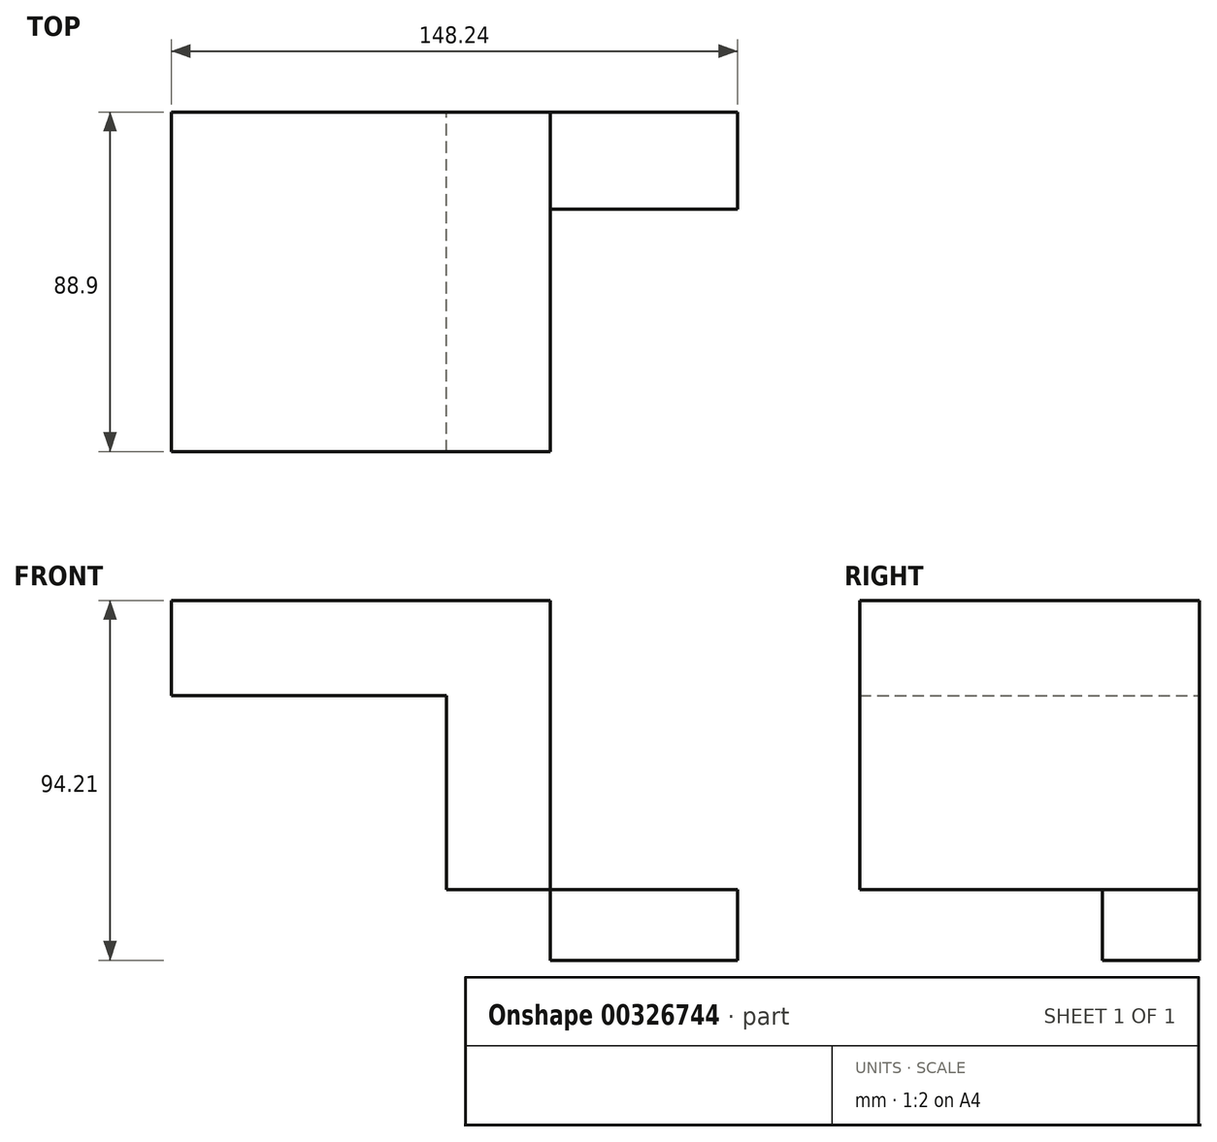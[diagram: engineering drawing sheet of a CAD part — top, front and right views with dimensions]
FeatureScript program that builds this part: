
annotation { "Feature Type Name" : "Feature", "Feature Type Description" : "" }
export const myFeature = defineFeature(function(context is Context, id is Id, definition is map)
    precondition{}
    {
        {
            var Q0;
            Q0=qCreatedBy(makeId("Front.planeOp"),FACE);
            var sketch = newSketch(context, id + "F0", { "sketchPlane" : qUnion([Q0])});
            skLineSegment(sketch, "E0", {"start": v(-75.82, 27.93) * mm, "end": v(-75.82, 3) * mm});
            skLineSegment(sketch, "E1", {"start": v(-75.82, 3) * mm, "end": v(-3.78, 3) * mm});
            skLineSegment(sketch, "E2", {"start": v(-3.78, 3) * mm, "end": v(-3.78, -47.8) * mm});
            skLineSegment(sketch, "E3", {"start": v(-3.78, -47.8) * mm, "end": v(72.42, -47.8) * mm});
            skLineSegment(sketch, "E4", {"start": v(72.42, -66.28) * mm, "end": v(72.42, -47.8) * mm});
            skLineSegment(sketch, "E5", {"start": v(72.42, -66.28) * mm, "end": v(23.47, -66.28) * mm});
            skLineSegment(sketch, "E6", {"start": v(23.47, -66.28) * mm, "end": v(23.47, 27.93) * mm});
            skLineSegment(sketch, "E7", {"start": v(-75.82, 27.93) * mm, "end": v(23.47, 27.93) * mm});
            skSolve(sketch);
        }
        {
            var Q0;
            Q0 = qSketchRegion(id + "F0", true);
            extrude(context, id + "F1", {"entities" : qUnion([Q0]), "depth" : 25.4 * mm});
        }
        {
            var Q0;
            Q0=makeQuery(id+"F1.opExtrude","CAP_FACE",FACE,{"disambiguationData":[OSD([sQuery(id+"F0.wireOp",EDGE,"E0"),sQuery(id+"F0.wireOp",EDGE,"E1"),sQuery(id+"F0.wireOp",EDGE,"E2"),sQuery(id+"F0.wireOp",EDGE,"E3"),sQuery(id+"F0.wireOp",EDGE,"E6"),sQuery(id+"F0.wireOp",EDGE,"E7")])],"isStart":false});
            extrude(context, id + "F2", {"entities" : qUnion([Q0]), "operationType" : NewBodyOperationType.ADD, "depth" : 63.5 * mm});
        }
    });
